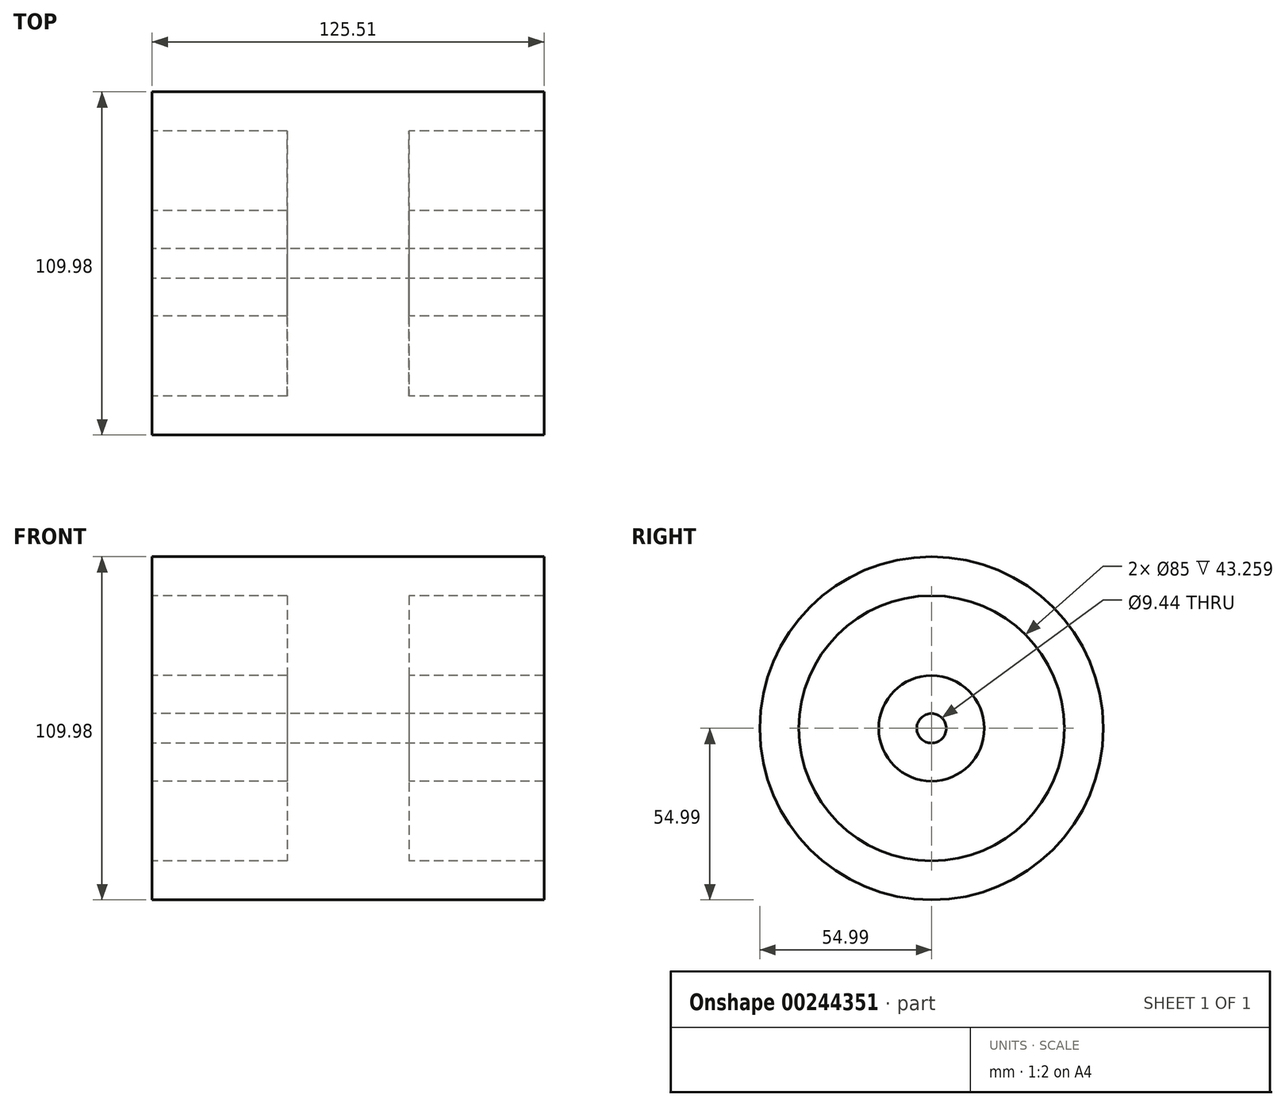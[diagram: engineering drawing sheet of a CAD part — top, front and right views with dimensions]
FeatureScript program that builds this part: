
annotation { "Feature Type Name" : "Feature", "Feature Type Description" : "" }
export const myFeature = defineFeature(function(context is Context, id is Id, definition is map)
    precondition{}
    {
        {
            var Q0;
            Q0=qCreatedBy(makeId("Front.planeOp"),FACE);
            var sketch = newSketch(context, id + "F0", { "sketchPlane" : qUnion([Q0])});
            skLineSegment(sketch, "E0", {"start": v(-104.19, 0) * mm, "end": v(104.19, 0) * mm, "construction": true});
            skLineSegment(sketch, "E1", {"start": v(0.3, 75.7) * mm, "end": v(0.3, -70.22) * mm, "construction": true});
            skPoint(sketch, "E1.startSnap0", {"position": v(0.3, 65.35) * mm});
            skLineSegment(sketch, "E2", {"start": v(0.3, 54.99) * mm, "end": v(63.06, 54.99) * mm});
            skLineSegment(sketch, "E3", {"start": v(63.06, 54.99) * mm, "end": v(63.06, 42.5) * mm});
            skLineSegment(sketch, "E4", {"start": v(63.06, 42.5) * mm, "end": v(19.8, 42.5) * mm});
            skLineSegment(sketch, "E5", {"start": v(19.8, 42.5) * mm, "end": v(19.8, 16.9) * mm});
            skLineSegment(sketch, "E6", {"start": v(19.8, 16.9) * mm, "end": v(63.06, 16.9) * mm});
            skLineSegment(sketch, "E7", {"start": v(63.06, 16.9) * mm, "end": v(63.06, 4.72) * mm});
            skLineSegment(sketch, "E8", {"start": v(63.06, 4.72) * mm, "end": v(0, 4.72) * mm});
            skLineSegment(sketch, "E9.MirrorCS", {"start": v(0.3, 54.99) * mm, "end": v(-62.45, 54.99) * mm});
            skLineSegment(sketch, "E10.MirrorCS", {"start": v(-62.45, 54.99) * mm, "end": v(-62.45, 42.5) * mm});
            skLineSegment(sketch, "E11.MirrorCS", {"start": v(-62.45, 42.5) * mm, "end": v(-19.2, 42.5) * mm});
            skLineSegment(sketch, "E12.MirrorCS", {"start": v(-19.2, 42.5) * mm, "end": v(-19.2, 16.9) * mm});
            skLineSegment(sketch, "E13.MirrorCS", {"start": v(-19.2, 16.9) * mm, "end": v(-62.45, 16.9) * mm});
            skLineSegment(sketch, "E14.MirrorCS", {"start": v(-62.45, 4.72) * mm, "end": v(0.6, 4.72) * mm});
            skLineSegment(sketch, "E15", {"start": v(-62.45, 4.72) * mm, "end": v(-62.45, 16.9) * mm});
            skSolve(sketch);
        }
        {
            var Q0;
            Q0 = qSketchRegion(id + "F0", true);
            var Q1;
            Q1=sQuery(id+"F0.wireOp",EDGE,"E0");
            revolve(context, id + "F1", {"entities" : qUnion([Q0]), "axis" : qUnion([Q1]), "revolveType" : RevolveType.FULL});
        }
    });
